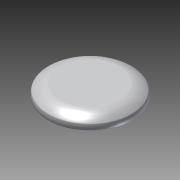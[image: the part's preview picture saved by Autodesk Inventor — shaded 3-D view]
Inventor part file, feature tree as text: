
AUTODESK INVENTOR PART (.ipt)
format: ipt  version: 2013 (Build 170138000, 138)  size: 161,792 bytes
history: native  units: in
note: dims shown in document units (in); Inventor stores cm internally (conversion verified against a paired STEP export)
features: fillet x4, sketch x2, extrude x1, revolve x1, projected_geometry x1
ambient origin geometry x8: Origin, YZ Plane, XZ Plane, XY Plane, X Axis, Y Axis, Z Axis, Center Point
bodies: Solid1 (feature_tree)
feature tree (9):
  extrude  "Extrusion1"  Depth=0.0938in TaperAngle=0.0deg
  revolve  "Revolution1"  Angle=90.0deg
  fillet  "Fillet1"  Radius=0.125in
  fillet  "Fillet2"  Radius=0.05in
  fillet  "Fillet3"  Radius=0.05in
  fillet  "Fillet4"  Radius=0.05in
  sketch  "Sketch1"  dims[d1=7.6875in d2=0.0938in d3=0.0in]
  sketch  "Sketch2"  dims[d14=0.75in d20=90.0deg d21=0.125in d22=0.05in d23=0.05in d24=0.05in]
  projected_geometry  "Projected Loop1"
